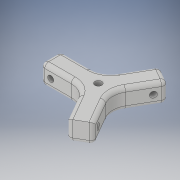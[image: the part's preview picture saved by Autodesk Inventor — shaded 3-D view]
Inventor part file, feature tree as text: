
AUTODESK INVENTOR PART (.ipt)
format: ipt  version: 2019 (Build 230136000, 136)  size: 209,920 bytes
history: native  units: mm
features: extrude x3, sketch x3, fillet x2, pattern_circular x1
ambient origin geometry x8: Origin, YZ Plane, XZ Plane, XY Plane, X Axis, Y Axis, Z Axis, Center Point
bodies: Body1 (feature_tree)
feature tree (9):
  extrude  "Extrusion7"  Depth=48.0mm
  extrude  "Extrusion8"  Depth=5.0mm
  extrude  "Extrusion9"  Depth=2.0mm
  pattern_circular  "Circular Pattern7"  [2 undecoded]
  fillet  "Fillet7"  Radius=30.0mm
  fillet  "Fillet8"  Radius=10.0mm
  sketch  "Sketch5"  dims[d54=3.5mm d78=48.0mm]
  sketch  "Sketch7"  dims[d82=5.0mm d83=5.0mm]
  sketch  "Sketch8"  dims[d84=90.0deg d85=24.0mm d86=10.0mm d87=30.0mm d89=360.0deg d91=10.0mm d92=0.0mm d93=5.0mm d94=5.0mm d95=3.0mm d96=20.0mm d97=0.0mm d98=3.5mm d99=10.0mm d100=0.0mm d101=30.0mm d102=360.0deg d104=10.0mm d105=2.0mm]
note: 2 required parameter values undecoded (feature->parameter linkage not recoverable at this tier; creation-order binding heuristic only, values carry confidence <= 0.55)
